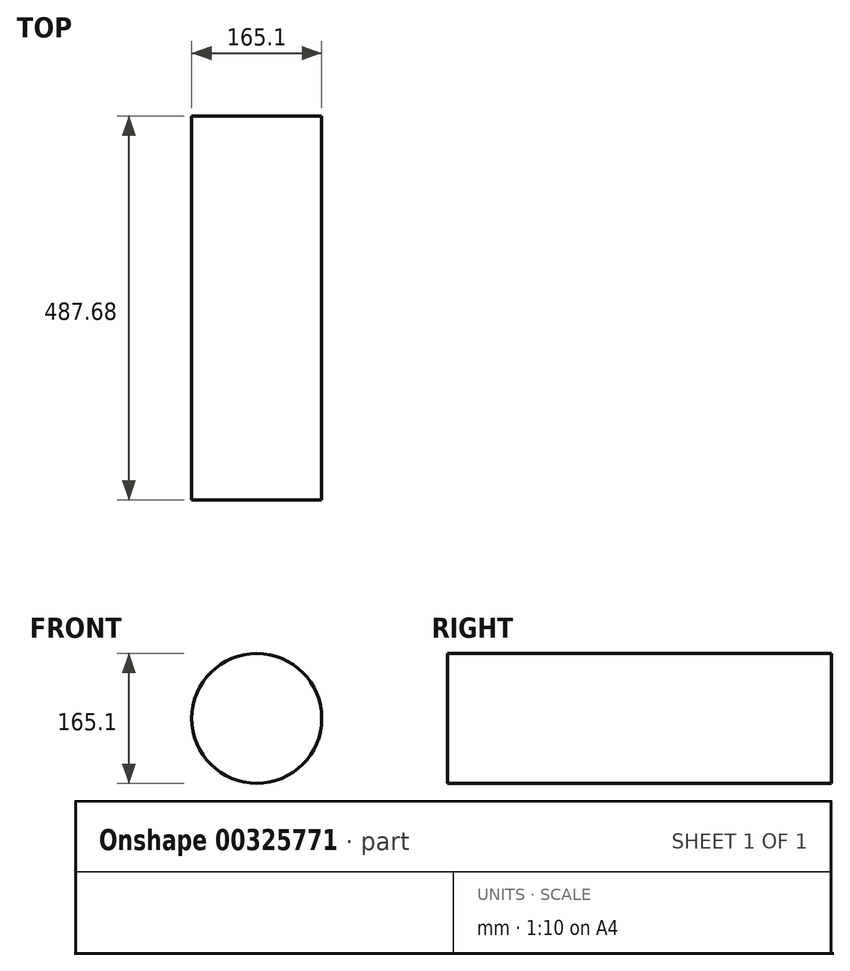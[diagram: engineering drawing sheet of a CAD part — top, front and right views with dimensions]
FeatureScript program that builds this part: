
annotation { "Feature Type Name" : "Feature", "Feature Type Description" : "" }
export const myFeature = defineFeature(function(context is Context, id is Id, definition is map)
    precondition{}
    {
        {
            var Q0;
            Q0=qCreatedBy(makeId("Front.planeOp"),FACE);
            var sketch = newSketch(context, id + "F0", { "sketchPlane" : qUnion([Q0])});
            skCircle(sketch, "E0", {"center": v(0, 0) * mm, "radius": 82.55 * mm});
            skSolve(sketch);
        }
        {
            var Q0;
            Q0=makeQuery(id+"F0.imprint","IMPRINT",FACE,{"disambiguationData":[TD([[makeQuery(id+"F0.imprint","IMPRINT",EDGE,{"derivedFrom":sQuery(id+"F0.wireOp",EDGE,"E0")}),1.0]])]});
            extrude(context, id + "F1", {"entities" : qUnion([Q0]), "depth" : 487.68 * mm});
        }
    });
